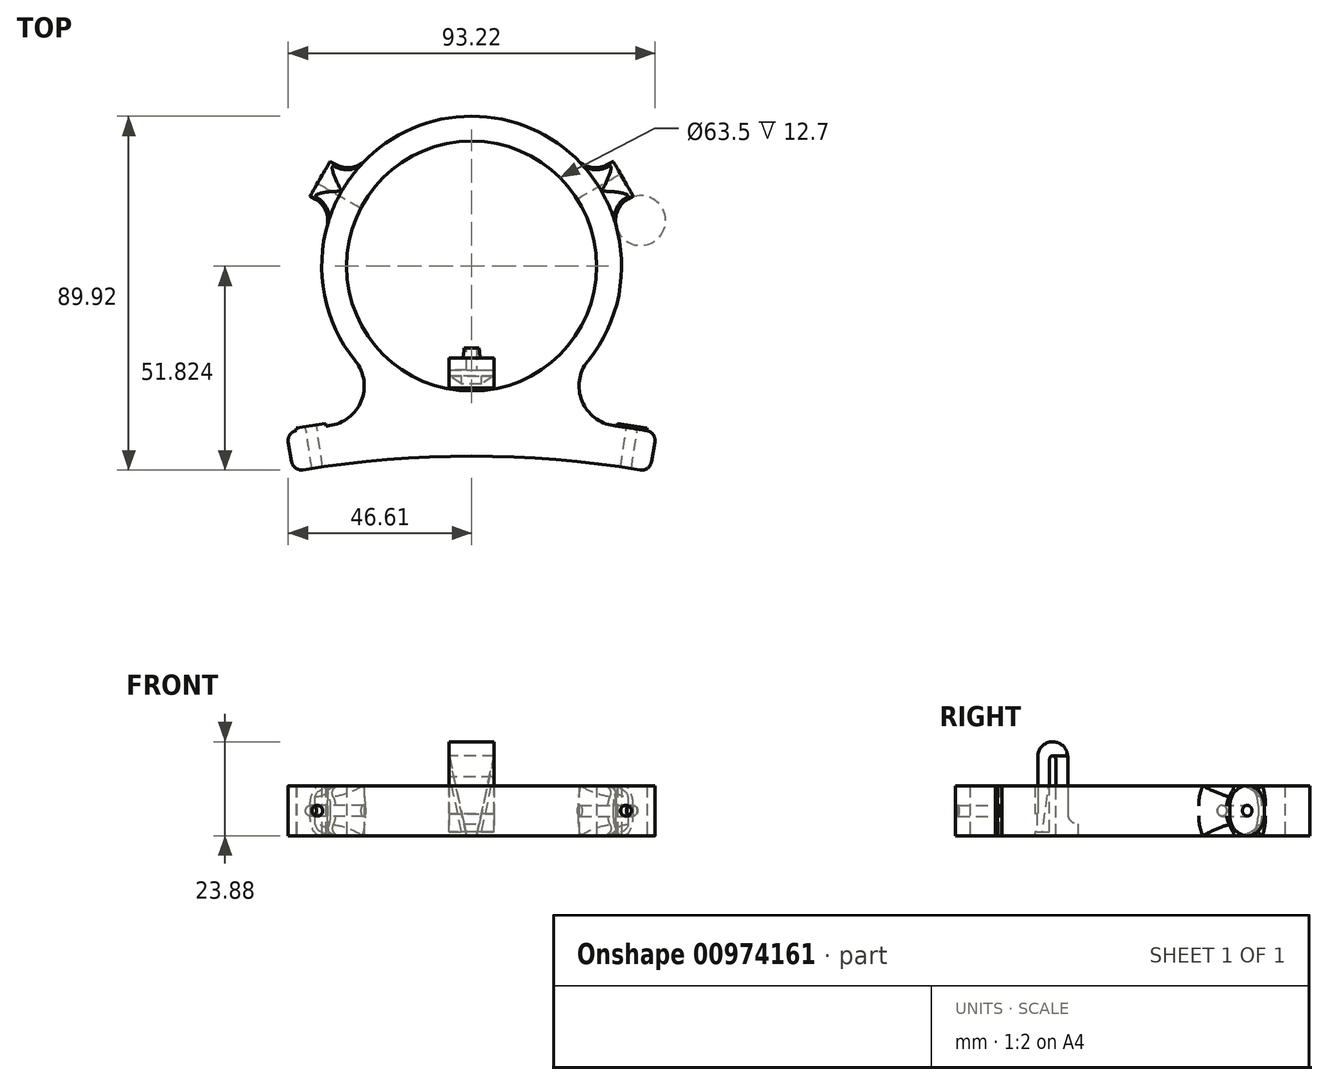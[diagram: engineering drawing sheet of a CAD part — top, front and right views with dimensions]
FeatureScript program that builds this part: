
annotation { "Feature Type Name" : "Feature", "Feature Type Description" : "" }
export const myFeature = defineFeature(function(context is Context, id is Id, definition is map)
    precondition{}
    {
        {
            var Q0;
            Q0=qCreatedBy(makeId("Top.planeOp"),FACE);
            var sketch = newSketch(context, id + "F0", { "sketchPlane" : qUnion([Q0])});
            skArc(sketch, "E0", {"start": v(-42.77, 257.07) * mm, "mid": v(0, 260.6) * mm, "end": v(42.77, 257.07) * mm});
            skLineSegment(sketch, "E1", {"start": v(0, 260.6) * mm, "end": v(0, 0) * mm});
            skLineSegment(sketch, "E2", {"start": v(0, 0) * mm, "end": v(45.25, 256.64) * mm});
            skLineSegment(sketch, "E3", {"start": v(-45.25, 256.64) * mm, "end": v(0, 0) * mm});
            skArc(sketch, "E4", {"start": v(-44.5, 267.08) * mm, "mid": v(0, 270.76) * mm, "end": v(44.5, 267.08) * mm});
            skLineSegment(sketch, "E5", {"start": v(45.7, 259.13) * mm, "end": v(46.57, 264.14) * mm});
            skLineSegment(sketch, "E6", {"start": v(-45.7, 259.13) * mm, "end": v(-46.57, 264.14) * mm});
            skPoint(sketch, "E7.visualSharp", {"position": v(-47.02, 266.65) * mm});
            skArc(sketch, "E7.filletArc", {"start": v(-44.5, 267.08) * mm, "mid": v(-46.15, 266.05) * mm, "end": v(-46.57, 264.14) * mm});
            skPoint(sketch, "E8.visualSharp", {"position": v(-45.25, 256.64) * mm});
            skArc(sketch, "E8.filletArc", {"start": v(-45.7, 259.13) * mm, "mid": v(-44.66, 257.5) * mm, "end": v(-42.77, 257.07) * mm});
            skPoint(sketch, "E9.visualSharp", {"position": v(47.02, 266.65) * mm});
            skArc(sketch, "E9.filletArc", {"start": v(46.57, 264.14) * mm, "mid": v(46.15, 266.05) * mm, "end": v(44.5, 267.08) * mm});
            skPoint(sketch, "E10.visualSharp", {"position": v(45.25, 256.64) * mm});
            skArc(sketch, "E10.filletArc", {"start": v(42.77, 257.07) * mm, "mid": v(44.66, 257.5) * mm, "end": v(45.7, 259.13) * mm});
            skLineSegment(sketch, "E11", {"start": v(0, 270.76) * mm, "end": v(0, 308.86) * mm, "construction": true});
            skCircle(sketch, "E12", {"center": v(0, 308.86) * mm, "radius": 31.75 * mm});
            skCircle(sketch, "E13", {"center": v(0, 308.86) * mm, "radius": 38.1 * mm});
            skLineSegment(sketch, "E14.bottom", {"start": v(-25.4, 269.57) * mm, "end": v(25.4, 269.57) * mm});
            skLineSegment(sketch, "E14.top", {"start": v(-25.4, 280.47) * mm, "end": v(25.4, 280.47) * mm});
            skLineSegment(sketch, "E14.left", {"start": v(-25.4, 269.57) * mm, "end": v(-25.4, 280.47) * mm});
            skLineSegment(sketch, "E14.right", {"start": v(25.4, 269.57) * mm, "end": v(25.4, 280.47) * mm});
            skLineSegment(sketch, "E15", {"start": v(0, 308.86) * mm, "end": v(38.5, 331.09) * mm, "construction": true});
            skLineSegment(sketch, "E16", {"start": v(38.5, 331.09) * mm, "end": v(35.95, 335.49) * mm});
            skLineSegment(sketch, "E17", {"start": v(38.5, 331.09) * mm, "end": v(41.03, 326.69) * mm});
            skLineSegment(sketch, "E18", {"start": v(35.95, 335.49) * mm, "end": v(30.16, 332.14) * mm});
            skLineSegment(sketch, "E19", {"start": v(41.03, 326.69) * mm, "end": v(35.24, 323.34) * mm});
            skLineSegment(sketch, "E20.MirrorCS", {"start": v(-35.95, 335.49) * mm, "end": v(-30.16, 332.14) * mm});
            skLineSegment(sketch, "E21.MirrorCS", {"start": v(-38.5, 331.09) * mm, "end": v(-35.95, 335.49) * mm});
            skLineSegment(sketch, "E22.MirrorCS", {"start": v(-38.5, 331.09) * mm, "end": v(-41.03, 326.69) * mm});
            skLineSegment(sketch, "E23.MirrorCS", {"start": v(-41.03, 326.69) * mm, "end": v(-35.24, 323.34) * mm});
            skLineSegment(sketch, "E24.MirrorCS", {"start": v(0, 308.86) * mm, "end": v(-38.5, 331.09) * mm, "construction": true});
            skLineSegment(sketch, "E25", {"start": v(36.96, 268.23) * mm, "end": v(44.5, 267.08) * mm});
            skLineSegment(sketch, "E26", {"start": v(36.96, 268.23) * mm, "end": v(37.05, 268.86) * mm});
            skLineSegment(sketch, "E27", {"start": v(37.05, 268.86) * mm, "end": v(44.59, 267.71) * mm});
            skLineSegment(sketch, "E28", {"start": v(44.59, 267.71) * mm, "end": v(44.5, 267.08) * mm});
            skLineSegment(sketch, "E29.MirrorCS", {"start": v(-36.96, 268.23) * mm, "end": v(-37.05, 268.86) * mm});
            skLineSegment(sketch, "E30.MirrorCS", {"start": v(-37.05, 268.86) * mm, "end": v(-44.59, 267.71) * mm});
            skLineSegment(sketch, "E31.MirrorCS", {"start": v(-44.59, 267.71) * mm, "end": v(-44.5, 267.08) * mm});
            skSolve(sketch);
        }
        {
            var Q0;
            {var subQ3=sQuery(id+"F0.wireOp",EDGE,"E14.left");Q0=makeQuery(id+"F0.imprint","IMPRINT",FACE,{"disambiguationData":[TD([[makeQuery(id+"F0.imprint","IMPRINT",EDGE,{"derivedFrom":subQ3}),-1.0]])]});}
            var Q1;
            Q1=makeQuery(id+"F0.imprint","IMPRINT",FACE,{"disambiguationData":[TD([[makeQuery(id+"F0.imprint","IMPRINT",EDGE,{"derivedFrom":sQuery(id+"F0.wireOp",EDGE,"E5")}),1.0]])]});
            var Q2;
            {var subQ3=sQuery(id+"F0.wireOp",EDGE,"E14.right");Q2=makeQuery(id+"F0.imprint","IMPRINT",FACE,{"disambiguationData":[TD([[makeQuery(id+"F0.imprint","IMPRINT",EDGE,{"derivedFrom":subQ3}),1.0]])]});}
            var Q3;
            {var subQ2=sQuery(id+"F0.wireOp",EDGE,"E14.bottom");Q3=makeQuery(id+"F0.imprint","IMPRINT",FACE,{"disambiguationData":[TD([[makeQuery(id+"F0.imprint","IMPRINT",EDGE,{"derivedFrom":subQ2}),1.0]])]});}
            var Q4;
            {var subQ1=sQuery(id+"F0.wireOp",EDGE,"E11");var subQ3=sQuery(id+"F0.wireOp",EDGE,"E12");var subQ4=makeQuery(id+"F0.imprint","INTERSECT",VERTEX,{"derivedFrom":[subQ1,subQ3]});Q4=makeQuery(id+"F0.imprint","IMPRINT",FACE,{"disambiguationData":[TD([[makeQuery(id+"F0.imprint","IMPRINT",EDGE,{"disambiguationData":[TD([[subQ4,-1.0]])],"derivedFrom":subQ3}),-1.0]])]});}
            var Q5;
            {var subQ1=sQuery(id+"F0.wireOp",EDGE,"E11");var subQ3=sQuery(id+"F0.wireOp",EDGE,"E12");var subQ4=makeQuery(id+"F0.imprint","INTERSECT",VERTEX,{"derivedFrom":[subQ1,subQ3]});Q5=makeQuery(id+"F0.imprint","IMPRINT",FACE,{"disambiguationData":[TD([[makeQuery(id+"F0.imprint","IMPRINT",EDGE,{"disambiguationData":[TD([[subQ4,1.0]])],"derivedFrom":subQ3}),-1.0]])]});}
            var Q6;
            {var subQ0=sQuery(id+"F0.wireOp",EDGE,"E14.top");var subQ1=sQuery(id+"F0.wireOp",EDGE,"E12");var subQ2=makeQuery(id+"F0.imprint","INTERSECT",VERTEX,{"disambiguationData":[OD(0.0)],"derivedFrom":[subQ1,subQ0]});Q6=makeQuery(id+"F0.imprint","IMPRINT",FACE,{"disambiguationData":[TD([[makeQuery(id+"F0.imprint","IMPRINT",EDGE,{"disambiguationData":[TD([[subQ2,1.0]])],"derivedFrom":subQ1}),-1.0]])]});}
            var Q7;
            Q7=makeQuery(id+"F0.imprint","IMPRINT",FACE,{"disambiguationData":[TD([[makeQuery(id+"F0.imprint","IMPRINT",EDGE,{"derivedFrom":sQuery(id+"F0.wireOp",EDGE,"E16")}),1.0]])]});
            var Q8;
            {var subQ0=sQuery(id+"F0.wireOp",EDGE,"E20.MirrorCS");Q8=makeQuery(id+"F0.imprint","IMPRINT",FACE,{"disambiguationData":[TD([[makeQuery(id+"F0.imprint","IMPRINT",EDGE,{"derivedFrom":subQ0}),-1.0]])]});}
            var Q9;
            {var subQ2=sQuery(id+"F0.wireOp",EDGE,"E29.MirrorCS");Q9=makeQuery(id+"F0.imprint","IMPRINT",FACE,{"disambiguationData":[TD([[makeQuery(id+"F0.imprint","IMPRINT",EDGE,{"derivedFrom":subQ2}),1.0]])]});}
            var Q10;
            {var subQ3=sQuery(id+"F0.wireOp",EDGE,"E26");Q10=makeQuery(id+"F0.imprint","IMPRINT",FACE,{"disambiguationData":[TD([[makeQuery(id+"F0.imprint","IMPRINT",EDGE,{"derivedFrom":subQ3}),-1.0]])]});}
            extrude(context, id + "F1", {"entities" : qUnion([Q0, Q1, Q2, Q3, Q4, Q5, Q6, Q7, Q8, Q9, Q10]), "depth" : 12.7 * mm, "offsetDistance" : 25.4 * mm});
        }
        {
            var Q0;
            Q0=makeQuery(id+"F1.opExtrude","SWEPT_EDGE",EDGE,{"disambiguationData":[OSD([sQuery(id+"F0.wireOp",EDGE,"E13"),sQuery(id+"F0.wireOp",EDGE,"E14.top"),sQuery(id+"F0.wireOp",EDGE,"E14.left")])]});
            var Q1;
            Q1=makeQuery(id+"F1.opExtrude","SWEPT_EDGE",EDGE,{"disambiguationData":[OSD([sQuery(id+"F0.wireOp",EDGE,"E13"),sQuery(id+"F0.wireOp",EDGE,"E14.top"),sQuery(id+"F0.wireOp",EDGE,"E14.right")])]});
            fillet(context, id + "F2", {"entities" : qUnion([Q0, Q1]), "radius" : 19.05 * mm, "tangentPropagation" : true, "allowEdgeOverflow" : false});
        }
        {
            var Q0;
            Q0=makeQuery(id+"F1.opExtrude","SWEPT_EDGE",EDGE,{"disambiguationData":[OSD([sQuery(id+"F0.wireOp",EDGE,"E4"),sQuery(id+"F0.wireOp",EDGE,"E14.bottom"),sQuery(id+"F0.wireOp",EDGE,"E14.left")])]});
            var Q1;
            Q1=makeQuery(id+"F1.opExtrude","SWEPT_EDGE",EDGE,{"disambiguationData":[OSD([sQuery(id+"F0.wireOp",EDGE,"E4"),sQuery(id+"F0.wireOp",EDGE,"E14.bottom"),sQuery(id+"F0.wireOp",EDGE,"E14.right")])]});
            fillet(context, id + "F3", {"entities" : qUnion([Q0, Q1]), "radius" : 10.16 * mm, "tangentPropagation" : true, "allowEdgeOverflow" : false});
        }
        {
            var Q0;
            Q0=makeQuery(id+"F1.opExtrude","CAP_EDGE",EDGE,{"disambiguationData":[OSD([sQuery(id+"F0.wireOp",EDGE,"E18")])],"isStart":true});
            var Q1;
            Q1=makeQuery(id+"F1.opExtrude","CAP_EDGE",EDGE,{"disambiguationData":[OSD([sQuery(id+"F0.wireOp",EDGE,"E18")])],"isStart":false});
            var Q2;
            Q2=makeQuery(id+"F1.opExtrude","CAP_EDGE",EDGE,{"disambiguationData":[OSD([sQuery(id+"F0.wireOp",EDGE,"E19")])],"isStart":false});
            var Q3;
            Q3=makeQuery(id+"F1.opExtrude","CAP_EDGE",EDGE,{"disambiguationData":[OSD([sQuery(id+"F0.wireOp",EDGE,"E19")])],"isStart":true});
            var Q4;
            Q4=makeQuery(id+"F1.opExtrude","CAP_EDGE",EDGE,{"disambiguationData":[OSD([sQuery(id+"F0.wireOp",EDGE,"E20.MirrorCS")])],"isStart":false});
            var Q5;
            Q5=makeQuery(id+"F1.opExtrude","CAP_EDGE",EDGE,{"disambiguationData":[OSD([sQuery(id+"F0.wireOp",EDGE,"E23.MirrorCS")])],"isStart":false});
            var Q6;
            Q6=makeQuery(id+"F1.opExtrude","CAP_EDGE",EDGE,{"disambiguationData":[OSD([sQuery(id+"F0.wireOp",EDGE,"E23.MirrorCS")])],"isStart":true});
            var Q7;
            Q7=makeQuery(id+"F1.opExtrude","CAP_EDGE",EDGE,{"disambiguationData":[OSD([sQuery(id+"F0.wireOp",EDGE,"E20.MirrorCS")])],"isStart":true});
            fillet(context, id + "F4", {"entities" : qUnion([Q0, Q1, Q2, Q3, Q4, Q5, Q6, Q7]), "radius" : 5.08 * mm, "tangentPropagation" : true, "allowEdgeOverflow" : false});
        }
        {
            var Q0;
            {var subQ0=sQuery(id+"F0.wireOp",EDGE,"E13");var subQ1=sQuery(id+"F0.wireOp",EDGE,"E20.MirrorCS");Q0=makeQuery(id+"F4.opFillet","BLEND_EDGE",EDGE,{"blendedFrom":[makeQuery(id+"F1.opExtrude","CAP_EDGE",EDGE,{"disambiguationData":[OSD([subQ1])],"isStart":false}),makeQuery(id+"F1.opExtrude","SWEPT_FACE",FACE,{"disambiguationData":[OSD([subQ0]),TDD([makeQuery(id+"F0.imprint","IMPRINT",EDGE,{"disambiguationData":[TD([[makeQuery(id+"F0.imprint","INTERSECT",VERTEX,{"derivedFrom":[subQ0,sQuery(id+"F0.wireOp",EDGE,"E18")]}),-1.0]])],"derivedFrom":subQ0})])]})],"blendedInto":[makeQuery(id+"F1.opExtrude","SWEPT_FACE",FACE,{"disambiguationData":[OSD([subQ0]),TDD([makeQuery(id+"F0.imprint","IMPRINT",EDGE,{"disambiguationData":[TD([[makeQuery(id+"F0.imprint","INTERSECT",VERTEX,{"derivedFrom":[subQ0,sQuery(id+"F0.wireOp",EDGE,"E18")]}),-1.0]])],"derivedFrom":subQ0})])]})]});}
            var Q1;
            {var subQ0=sQuery(id+"F0.wireOp",EDGE,"E13");var subQ1=sQuery(id+"F0.wireOp",EDGE,"E19");Q1=makeQuery(id+"F4.opFillet","BLEND_EDGE",EDGE,{"blendedFrom":[makeQuery(id+"F1.opExtrude","CAP_EDGE",EDGE,{"disambiguationData":[OSD([subQ1])],"isStart":false}),makeQuery(id+"F1.opExtrude","SWEPT_FACE",FACE,{"disambiguationData":[OSD([subQ0]),TDD([makeQuery(id+"F0.imprint","IMPRINT",EDGE,{"disambiguationData":[TD([[makeQuery(id+"F0.imprint","INTERSECT",VERTEX,{"derivedFrom":[subQ0,subQ1]}),1.0]])],"derivedFrom":subQ0})])]})],"blendedInto":[makeQuery(id+"F1.opExtrude","SWEPT_FACE",FACE,{"disambiguationData":[OSD([subQ0]),TDD([makeQuery(id+"F0.imprint","IMPRINT",EDGE,{"disambiguationData":[TD([[makeQuery(id+"F0.imprint","INTERSECT",VERTEX,{"derivedFrom":[subQ0,subQ1]}),1.0]])],"derivedFrom":subQ0})])]})]});}
            fillet(context, id + "F5", {"entities" : qUnion([Q0, Q1]), "radius" : 6.35 * mm, "tangentPropagation" : true, "allowEdgeOverflow" : false});
        }
        {
            var Q0;
            Q0=makeQuery(id+"F1.opExtrude","SWEPT_FACE",FACE,{"disambiguationData":[OSD([sQuery(id+"F0.wireOp",EDGE,"E16"),sQuery(id+"F0.wireOp",EDGE,"E17")])]});
            var sketch = newSketch(context, id + "F6", { "sketchPlane" : qUnion([Q0])});
            skLineSegment(sketch, "E32", {"start": v(267.48, 0) * mm, "end": v(267.48, 12.7) * mm, "construction": true});
            skLineSegment(sketch, "E33", {"start": v(272.56, 6.35) * mm, "end": v(262.4, 6.35) * mm, "construction": true});
            skCircle(sketch, "E34", {"center": v(267.48, 6.35) * mm, "radius": 1.4 * mm});
            skSolve(sketch);
        }
        {
            var Q0;
            Q0=makeQuery(id+"F6.imprint","IMPRINT",FACE,{"disambiguationData":[TD([[makeQuery(id+"F6.imprint","IMPRINT",EDGE,{"derivedFrom":sQuery(id+"F6.wireOp",EDGE,"E34")}),1.0]])]});
            extrude(context, id + "F7", {"entities" : qUnion([Q0]), "operationType" : NewBodyOperationType.REMOVE, "oppositeDirection" : true, "depth" : 50.8 * mm, "offsetDistance" : 25.4 * mm});
        }
        {
            var Q0;
            Q0=makeQuery(id+"F1.opExtrude","SWEPT_FACE",FACE,{"disambiguationData":[OSD([sQuery(id+"F0.wireOp",EDGE,"E21.MirrorCS"),sQuery(id+"F0.wireOp",EDGE,"E22.MirrorCS")])]});
            var sketch = newSketch(context, id + "F8", { "sketchPlane" : qUnion([Q0])});
            skLineSegment(sketch, "E35", {"start": v(-267.48, 0) * mm, "end": v(-267.48, 12.7) * mm, "construction": true});
            skLineSegment(sketch, "E36", {"start": v(-272.56, 6.35) * mm, "end": v(-262.4, 6.35) * mm, "construction": true});
            skCircle(sketch, "E37", {"center": v(-267.48, 6.35) * mm, "radius": 1.4 * mm});
            skSolve(sketch);
        }
        {
            var Q0;
            Q0=makeQuery(id+"F8.imprint","IMPRINT",FACE,{"disambiguationData":[TD([[makeQuery(id+"F8.imprint","IMPRINT",EDGE,{"derivedFrom":sQuery(id+"F8.wireOp",EDGE,"E37")}),1.0]])]});
            extrude(context, id + "F9", {"entities" : qUnion([Q0]), "operationType" : NewBodyOperationType.REMOVE, "oppositeDirection" : true, "depth" : 50.8 * mm, "offsetDistance" : 25.4 * mm});
        }
        {
            var Q0;
            Q0=makeQuery(id+"F1.opExtrude","SWEPT_FACE",FACE,{"disambiguationData":[OSD([sQuery(id+"F0.wireOp",EDGE,"E30.MirrorCS")])]});
            var sketch = newSketch(context, id + "F10", { "sketchPlane" : qUnion([Q0])});
            skCircle(sketch, "E38", {"center": v(0, 6.35) * mm, "radius": 1.4 * mm});
            skPoint(sketch, "E38.centerSnap0", {"position": v(-3.81, 6.35) * mm});
            skSolve(sketch);
        }
        {
            var Q0;
            Q0=makeQuery(id+"F1.opExtrude","SWEPT_FACE",FACE,{"disambiguationData":[OSD([sQuery(id+"F0.wireOp",EDGE,"E27")])]});
            var sketch = newSketch(context, id + "F11", { "sketchPlane" : qUnion([Q0])});
            skCircle(sketch, "E39", {"center": v(0, 6.35) * mm, "radius": 1.4 * mm});
            skPoint(sketch, "E39.centerSnap0", {"position": v(-3.8, 6.35) * mm});
            skSolve(sketch);
        }
        {
            var Q0;
            Q0=makeQuery(id+"F11.imprint","IMPRINT",FACE,{"disambiguationData":[TD([[makeQuery(id+"F11.imprint","IMPRINT",EDGE,{"derivedFrom":sQuery(id+"F11.wireOp",EDGE,"E39")}),1.0]])]});
            extrude(context, id + "F12", {"entities" : qUnion([Q0]), "operationType" : NewBodyOperationType.REMOVE, "oppositeDirection" : true, "depth" : 25.4 * mm, "offsetDistance" : 25.4 * mm});
        }
        {
            var Q0;
            Q0=makeQuery(id+"F10.imprint","IMPRINT",FACE,{"disambiguationData":[TD([[makeQuery(id+"F10.imprint","IMPRINT",EDGE,{"derivedFrom":sQuery(id+"F10.wireOp",EDGE,"E38")}),1.0]])]});
            extrude(context, id + "F13", {"entities" : qUnion([Q0]), "operationType" : NewBodyOperationType.REMOVE, "oppositeDirection" : true, "depth" : 25.4 * mm, "offsetDistance" : 25.4 * mm});
        }
        {
            var Q0;
            Q0=makeQuery(id+"F1.opExtrude","CAP_FACE",FACE,{"disambiguationData":[OSD([sQuery(id+"F0.wireOp",EDGE,"E0"),sQuery(id+"F0.wireOp",EDGE,"E4"),sQuery(id+"F0.wireOp",EDGE,"E5"),sQuery(id+"F0.wireOp",EDGE,"E6"),sQuery(id+"F0.wireOp",EDGE,"E7.filletArc"),sQuery(id+"F0.wireOp",EDGE,"E8.filletArc"),sQuery(id+"F0.wireOp",EDGE,"E9.filletArc"),sQuery(id+"F0.wireOp",EDGE,"E10.filletArc"),sQuery(id+"F0.wireOp",EDGE,"E12"),sQuery(id+"F0.wireOp",EDGE,"E13"),sQuery(id+"F0.wireOp",EDGE,"E14.left"),sQuery(id+"F0.wireOp",EDGE,"E14.right"),sQuery(id+"F0.wireOp",EDGE,"E16"),sQuery(id+"F0.wireOp",EDGE,"E17"),sQuery(id+"F0.wireOp",EDGE,"E18"),sQuery(id+"F0.wireOp",EDGE,"E19"),sQuery(id+"F0.wireOp",EDGE,"E20.MirrorCS"),sQuery(id+"F0.wireOp",EDGE,"E21.MirrorCS"),sQuery(id+"F0.wireOp",EDGE,"E22.MirrorCS"),sQuery(id+"F0.wireOp",EDGE,"E23.MirrorCS"),sQuery(id+"F0.wireOp",EDGE,"E25"),sQuery(id+"F0.wireOp",EDGE,"E29.MirrorCS"),sQuery(id+"F0.wireOp",EDGE,"E30.MirrorCS"),sQuery(id+"F0.wireOp",EDGE,"E31.MirrorCS")])],"isStart":true});
            var sketch = newSketch(context, id + "F14", { "sketchPlane" : qUnion([Q0])});
            skLineSegment(sketch, "E40", {"start": v(0, -260.6) * mm, "end": v(0, -277.11) * mm});
            skSolve(sketch);
        }
        {
            var Q0;
            Q0=sQuery(id+"F14.wireOp",EDGE,"E40");
            extrude(context, id + "F15", {"bodyType" : ToolBodyType.SURFACE, "surfaceEntities" : qUnion([Q0]), "depth" : 0.03 * mm, "offsetDistance" : 25.4 * mm});
        }
        {
            var Q0;
            Q0=makeQuery(id+"F15.opExtrude","SWEPT_FACE",FACE,{"disambiguationData":[OSD([sQuery(id+"F14.wireOp",EDGE,"E40")])]});
            var sketch = newSketch(context, id + "F16", { "sketchPlane" : qUnion([Q0])});
            skLineSegment(sketch, "E41", {"start": v(-340.61, 0) * mm, "end": v(-340.61, 12.7) * mm});
            skLineSegment(sketch, "E42", {"start": v(-268.86, -0.03) * mm, "end": v(-271.34, -0.03) * mm});
            skLineSegment(sketch, "E43", {"start": v(-277.11, 12.7) * mm, "end": v(-277.11, 1.02) * mm});
            skLineSegment(sketch, "E44", {"start": v(-277.11, 1.02) * mm, "end": v(-277.88, 1.02) * mm});
            skLineSegment(sketch, "E45", {"start": v(-277.11, 1.02) * mm, "end": v(-277.11, 5.59) * mm});
            skLineSegment(sketch, "E46", {"start": v(-277.11, 5.59) * mm, "end": v(-277.88, 5.59) * mm});
            skLineSegment(sketch, "E47", {"start": v(-277.88, 1.02) * mm, "end": v(-280.92, 1.02) * mm});
            skLineSegment(sketch, "E48", {"start": v(-280.92, 1.02) * mm, "end": v(-280.92, 23.88) * mm});
            skLineSegment(sketch, "E49", {"start": v(-280.92, 23.88) * mm, "end": v(-277.88, 23.88) * mm});
            skLineSegment(sketch, "E50", {"start": v(-277.88, 23.88) * mm, "end": v(-277.88, 5.59) * mm});
            skLineSegment(sketch, "E51.bottom", {"start": v(-280.92, 23.88) * mm, "end": v(-285.5, 23.88) * mm});
            skLineSegment(sketch, "E51.top", {"start": v(-280.92, 20.32) * mm, "end": v(-285.5, 20.32) * mm});
            skLineSegment(sketch, "E51.left", {"start": v(-280.92, 23.88) * mm, "end": v(-280.92, 20.32) * mm});
            skLineSegment(sketch, "E51.right", {"start": v(-285.5, 23.88) * mm, "end": v(-285.5, 20.32) * mm});
            skLineSegment(sketch, "E52.bottom", {"start": v(-285.5, 20.32) * mm, "end": v(-282.45, 20.32) * mm});
            skLineSegment(sketch, "E52.top", {"start": v(-285.5, 0) * mm, "end": v(-282.45, 0) * mm});
            skLineSegment(sketch, "E52.left", {"start": v(-285.5, 20.32) * mm, "end": v(-285.5, 0) * mm});
            skLineSegment(sketch, "E52.right", {"start": v(-282.45, 20.32) * mm, "end": v(-282.45, 0) * mm});
            skLineSegment(sketch, "E53.bottom", {"start": v(-285.5, 0) * mm, "end": v(-288.04, 0) * mm});
            skLineSegment(sketch, "E53.top", {"start": v(-285.5, 3.05) * mm, "end": v(-288.04, 3.05) * mm});
            skLineSegment(sketch, "E53.left", {"start": v(-285.5, 0) * mm, "end": v(-285.5, 3.05) * mm});
            skLineSegment(sketch, "E53.right", {"start": v(-288.04, 0) * mm, "end": v(-288.04, 3.05) * mm});
            skSolve(sketch);
        }
        {
            var Q0;
            {var subQ0=sQuery(id+"F16.wireOp",EDGE,"E53.bottom");Q0=makeQuery(id+"F16.imprint","IMPRINT",FACE,{"disambiguationData":[TD([[makeQuery(id+"F16.imprint","IMPRINT",EDGE,{"derivedFrom":subQ0}),-1.0]])]});}
            var Q1;
            {var subQ4=sQuery(id+"F16.wireOp",EDGE,"E52.top");Q1=makeQuery(id+"F16.imprint","IMPRINT",FACE,{"disambiguationData":[TD([[makeQuery(id+"F16.imprint","IMPRINT",EDGE,{"derivedFrom":subQ4}),1.0]])]});}
            var Q2;
            {var subQ2=sQuery(id+"F16.wireOp",EDGE,"E44");Q2=makeQuery(id+"F16.imprint","IMPRINT",FACE,{"disambiguationData":[TD([[makeQuery(id+"F16.imprint","IMPRINT",EDGE,{"derivedFrom":subQ2}),-1.0]])]});}
            var Q3;
            {var subQ3=sQuery(id+"F16.wireOp",EDGE,"E51.bottom");Q3=makeQuery(id+"F16.imprint","IMPRINT",FACE,{"disambiguationData":[TD([[makeQuery(id+"F16.imprint","IMPRINT",EDGE,{"derivedFrom":subQ3}),1.0]])]});}
            extrude(context, id + "F17", {"entities" : qUnion([Q0, Q1, Q2, Q3]), "operationType" : NewBodyOperationType.ADD, "endBound" : BoundingType.SYMMETRIC, "depth" : 11.43 * mm, "offsetDistance" : 25.4 * mm});
        }
        {
            var Q0;
            Q0=makeQuery(id+"F17.opExtrude","SWEPT_EDGE",EDGE,{"disambiguationData":[OSD([sQuery(id+"F16.wireOp",EDGE,"E51.bottom"),sQuery(id+"F16.wireOp",EDGE,"E51.right")])]});
            var Q1;
            Q1=makeQuery(id+"F17.opExtrude","SWEPT_EDGE",EDGE,{"disambiguationData":[OSD([sQuery(id+"F16.wireOp",EDGE,"E49"),sQuery(id+"F16.wireOp",EDGE,"E50")])]});
            fillet(context, id + "F18", {"entities" : qUnion([Q0, Q1]), "radius" : 3.8 * mm, "tangentPropagation" : true, "allowEdgeOverflow" : false});
        }
        {
            var Q0;
            Q0=makeQuery(id+"F17.opExtrude","SWEPT_EDGE",EDGE,{"disambiguationData":[OSD([sQuery(id+"F16.wireOp",EDGE,"E48"),sQuery(id+"F16.wireOp",EDGE,"E51.top")])]});
            var Q1;
            Q1=makeQuery(id+"F17.opExtrude","SWEPT_EDGE",EDGE,{"disambiguationData":[OSD([sQuery(id+"F16.wireOp",EDGE,"E51.top"),sQuery(id+"F16.wireOp",EDGE,"E52.right")])]});
            fillet(context, id + "F19", {"entities" : qUnion([Q0, Q1]), "radius" : 0.76 * mm, "tangentPropagation" : true, "allowEdgeOverflow" : false});
        }
        {
            var Q0;
            Q0=makeQuery(id+"F17.opExtrude","SWEPT_EDGE",EDGE,{"disambiguationData":[OSD([sQuery(id+"F16.wireOp",EDGE,"E46"),sQuery(id+"F16.wireOp",EDGE,"E50")])]});
            fillet(context, id + "F20", {"entities" : qUnion([Q0]), "radius" : 0.13 * mm, "allowEdgeOverflow" : false});
        }
        {
            var Q0;
            Q0=makeQuery(id+"F17.opExtrude","SWEPT_EDGE",EDGE,{"disambiguationData":[OSD([sQuery(id+"F16.wireOp",EDGE,"E52.left"),sQuery(id+"F16.wireOp",EDGE,"E53.top")])]});
            fillet(context, id + "F21", {"entities" : qUnion([Q0]), "radius" : 2.54 * mm, "tangentPropagation" : true, "allowEdgeOverflow" : false});
        }
        {
            var Q0;
            Q0=makeQuery(id+"F17.opExtrude","CAP_EDGE",EDGE,{"disambiguationData":[OSD([sQuery(id+"F16.wireOp",EDGE,"E52.top"),sQuery(id+"F16.wireOp",EDGE,"E53.bottom")])],"isStart":true});
            var Q1;
            Q1=makeQuery(id+"F17.opExtrude","CAP_EDGE",EDGE,{"disambiguationData":[OSD([sQuery(id+"F16.wireOp",EDGE,"E52.top"),sQuery(id+"F16.wireOp",EDGE,"E53.bottom")])],"isStart":false});
            chamfer(context, id + "F22", {"entities" : qUnion([Q0, Q1]), "chamferType" : ChamferType.TWO_OFFSETS, "width1" : 20.32 * mm, "oppositeDirection" : false, "width2" : 4.44 * mm, "tangentPropagation" : true});
        }
        {
            var Q0;
            Q0=makeQuery(id+"F17.opExtrude","SWEPT_FACE",FACE,{"disambiguationData":[OSD([sQuery(id+"F16.wireOp",EDGE,"E48")])]});
            var sketch = newSketch(context, id + "F23", { "sketchPlane" : qUnion([Q0])});
            skLineSegment(sketch, "E54.0", {"start": v(5.55, 19.56) * mm, "end": v(1.27, 0) * mm});
            skLineSegment(sketch, "E55.0", {"start": v(-1.27, 0) * mm, "end": v(-5.55, 19.56) * mm});
            skLineSegment(sketch, "E56.0", {"start": v(1.27, 0) * mm, "end": v(-1.27, 0) * mm});
            skLineSegment(sketch, "E57", {"start": v(-1.27, 0) * mm, "end": v(-2.29, 0) * mm});
            skLineSegment(sketch, "E58", {"start": v(1.27, 0) * mm, "end": v(2.29, 0) * mm});
            skLineSegment(sketch, "E59", {"start": v(-2.29, 0) * mm, "end": v(-5.54, 14.89) * mm});
            skLineSegment(sketch, "E60", {"start": v(2.29, 0) * mm, "end": v(5.54, 14.89) * mm});
            skLineSegment(sketch, "E61", {"start": v(-5.54, 14.89) * mm, "end": v(5.54, 14.89) * mm});
            skSolve(sketch);
        }
        {
            var Q0;
            {var subQ0=sQuery(id+"F23.wireOp",EDGE,"E61");var subQ5=sQuery(id+"F23.wireOp",EDGE,"E59");var subQ6=makeQuery(id+"F23.imprint","INTERSECT",VERTEX,{"derivedFrom":[subQ5,subQ0]});Q0=makeQuery(id+"F23.imprint","IMPRINT",FACE,{"disambiguationData":[TD([[makeQuery(id+"F23.imprint","IMPRINT",EDGE,{"disambiguationData":[TD([[subQ6,-1.0]])],"derivedFrom":subQ0}),-1.0]])]});}
            var Q1;
            {var subQ0=sQuery(id+"F23.wireOp",EDGE,"E56.0");Q1=makeQuery(id+"F23.imprint","IMPRINT",FACE,{"disambiguationData":[TD([[makeQuery(id+"F23.imprint","IMPRINT",EDGE,{"derivedFrom":subQ0}),-1.0]])]});}
            var Q2;
            {var subQ0=sQuery(id+"F23.wireOp",EDGE,"E58");Q2=makeQuery(id+"F23.imprint","IMPRINT",FACE,{"disambiguationData":[TD([[makeQuery(id+"F23.imprint","IMPRINT",EDGE,{"derivedFrom":subQ0}),1.0]])]});}
            var Q3;
            {var subQ0=sQuery(id+"F23.wireOp",EDGE,"E61");var subQ5=sQuery(id+"F23.wireOp",EDGE,"E60");var subQ6=makeQuery(id+"F23.imprint","INTERSECT",VERTEX,{"derivedFrom":[subQ5,subQ0]});Q3=makeQuery(id+"F23.imprint","IMPRINT",FACE,{"disambiguationData":[TD([[makeQuery(id+"F23.imprint","IMPRINT",EDGE,{"disambiguationData":[TD([[subQ6,1.0]])],"derivedFrom":subQ0}),-1.0]])]});}
            var Q4;
            {var subQ0=sQuery(id+"F23.wireOp",EDGE,"E61");var subQ1=sQuery(id+"F23.wireOp",EDGE,"E54.0");var subQ2=makeQuery(id+"F23.imprint","INTERSECT",VERTEX,{"derivedFrom":[subQ1,subQ0]});Q4=makeQuery(id+"F23.imprint","IMPRINT",FACE,{"disambiguationData":[TD([[makeQuery(id+"F23.imprint","IMPRINT",EDGE,{"disambiguationData":[TD([[subQ2,1.0]])],"derivedFrom":subQ0}),-1.0]])]});}
            var Q5;
            {var subQ0=sQuery(id+"F23.wireOp",EDGE,"E57");Q5=makeQuery(id+"F23.imprint","IMPRINT",FACE,{"disambiguationData":[TD([[makeQuery(id+"F23.imprint","IMPRINT",EDGE,{"derivedFrom":subQ0}),-1.0]])]});}
            extrude(context, id + "F24", {"entities" : qUnion([Q0, Q1, Q2, Q3, Q4, Q5]), "operationType" : NewBodyOperationType.REMOVE, "oppositeDirection" : true, "depth" : 2.54 * mm, "offsetDistance" : 25.4 * mm});
        }
        {
            var Q0;
            Q0=makeQuery(id+"F24.boolean.opBoolean","COPY",EDGE,{"derivedFrom":makeQuery(id+"F24.opExtrude","CAP_EDGE",EDGE,{"disambiguationData":[OSD([sQuery(id+"F23.wireOp",EDGE,"E61")])],"isStart":false})});
            chamfer(context, id + "F25", {"entities" : qUnion([Q0]), "chamferType" : ChamferType.TWO_OFFSETS, "width1" : 2.54 * mm, "oppositeDirection" : false, "width2" : 17.78 * mm, "tangentPropagation" : true});
        }
    });
